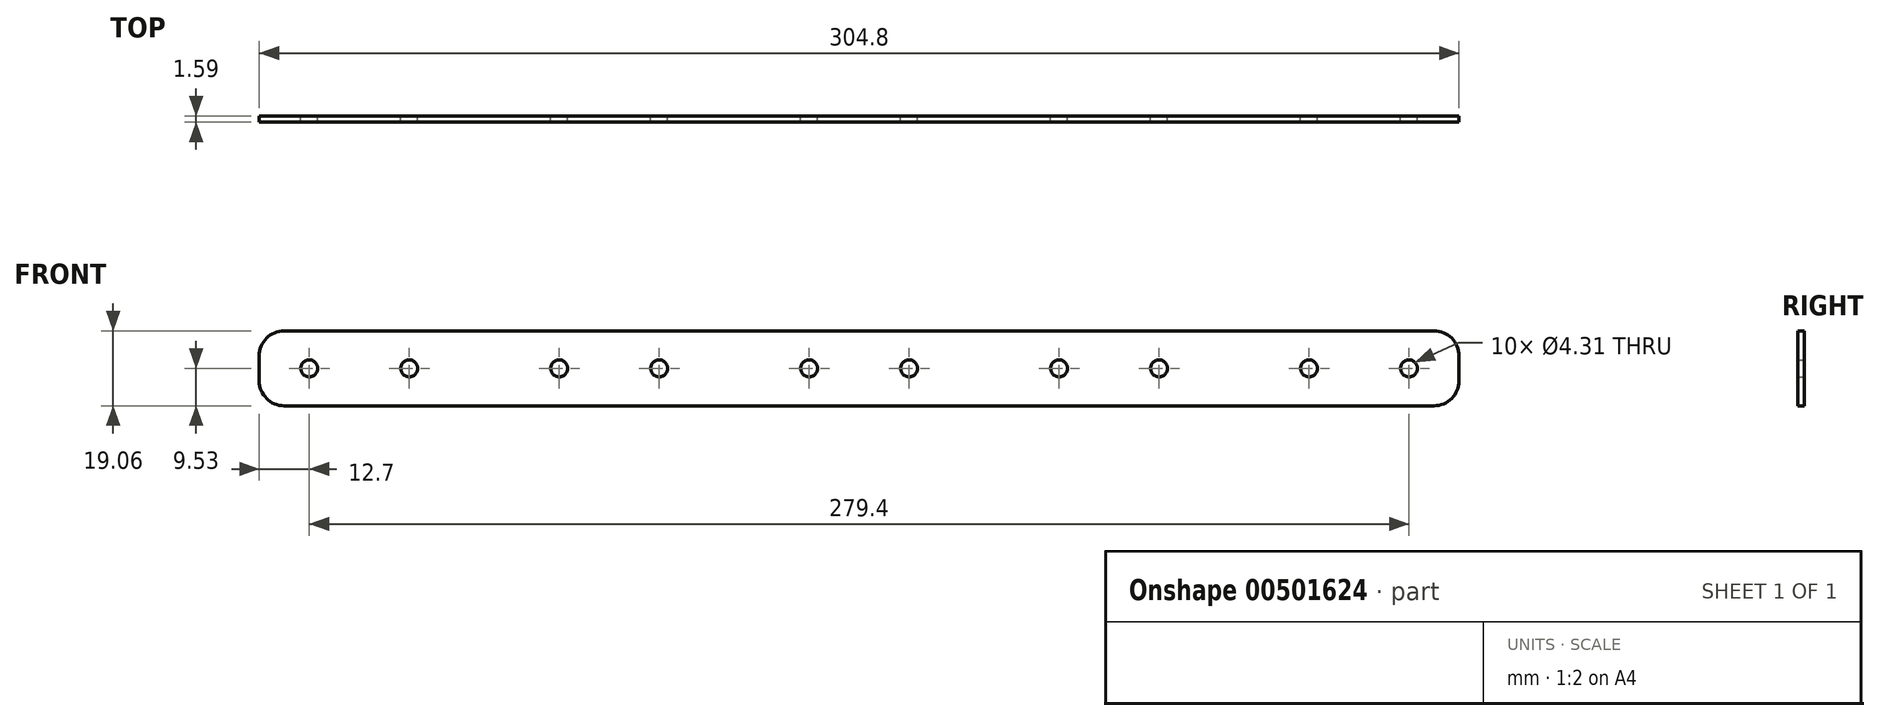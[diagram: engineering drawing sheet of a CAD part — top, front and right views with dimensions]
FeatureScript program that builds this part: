
annotation { "Feature Type Name" : "Feature", "Feature Type Description" : "" }
export const myFeature = defineFeature(function(context is Context, id is Id, definition is map)
    precondition{}
    {
        {
            var Q0;
            Q0=qCreatedBy(makeId("Front.planeOp"),FACE);
            var sketch = newSketch(context, id + "F0", { "sketchPlane" : qUnion([Q0])});
            skLineSegment(sketch, "E0.bottom", {"start": v(-146.05, 9.52) * mm, "end": v(146.05, 9.52) * mm});
            skLineSegment(sketch, "E0.top", {"start": v(-146.05, -9.53) * mm, "end": v(146.05, -9.53) * mm});
            skLineSegment(sketch, "E0.left", {"start": v(-152.4, 3.17) * mm, "end": v(-152.4, -3.18) * mm});
            skLineSegment(sketch, "E0.right", {"start": v(152.4, 3.17) * mm, "end": v(152.4, -3.18) * mm});
            skPoint(sketch, "E0.middle", {"position": v(0, 0) * mm});
            skCircle(sketch, "E1", {"center": v(-12.7, 0) * mm, "radius": 2.15 * mm});
            skCircle(sketch, "E2.MirrorC", {"center": v(12.7, 0) * mm, "radius": 2.15 * mm});
            skPoint(sketch, "E3.visualSharp", {"position": v(-152.4, 9.52) * mm});
            skArc(sketch, "E3.filletArc", {"start": v(-146.05, 9.52) * mm, "mid": v(-150.54, 7.67) * mm, "end": v(-152.4, 3.17) * mm});
            skPoint(sketch, "E4.visualSharp", {"position": v(-152.4, -9.53) * mm});
            skArc(sketch, "E4.filletArc", {"start": v(-152.4, -3.18) * mm, "mid": v(-150.54, -7.67) * mm, "end": v(-146.05, -9.53) * mm});
            skPoint(sketch, "E5.visualSharp", {"position": v(152.4, 9.52) * mm});
            skArc(sketch, "E5.filletArc", {"start": v(152.4, 3.17) * mm, "mid": v(150.54, 7.67) * mm, "end": v(146.05, 9.52) * mm});
            skPoint(sketch, "E6.visualSharp", {"position": v(152.4, -9.53) * mm});
            skArc(sketch, "E6.filletArc", {"start": v(146.05, -9.53) * mm, "mid": v(150.54, -7.67) * mm, "end": v(152.4, -3.18) * mm});
            skCircle(sketch, "E7.1.0.0", {"center": v(50.8, 0) * mm, "radius": 2.15 * mm});
            skCircle(sketch, "E7.1.0.1", {"center": v(76.2, 0) * mm, "radius": 2.15 * mm});
            skLineSegment(sketch, "E7.1.0.2", {"start": v(-82.55, -9.53) * mm, "end": v(209.55, -9.53) * mm});
            skCircle(sketch, "E7.2.0.0", {"center": v(114.3, 0) * mm, "radius": 2.15 * mm});
            skCircle(sketch, "E7.2.0.1", {"center": v(139.7, 0) * mm, "radius": 2.15 * mm});
            skLineSegment(sketch, "E7.2.0.2", {"start": v(-19.05, -9.53) * mm, "end": v(273.05, -9.53) * mm});
            skLineSegment(sketch, "E7.direction1", {"start": v(-12.7, 0) * mm, "end": v(50.8, 0) * mm, "construction": true});
            skCircle(sketch, "E8.MirrorC", {"center": v(-76.2, 0) * mm, "radius": 2.15 * mm});
            skCircle(sketch, "E9.MirrorC", {"center": v(-50.8, 0) * mm, "radius": 2.15 * mm});
            skCircle(sketch, "E10.MirrorC", {"center": v(-114.3, 0) * mm, "radius": 2.15 * mm});
            skCircle(sketch, "E11.MirrorC", {"center": v(-139.7, 0) * mm, "radius": 2.15 * mm});
            skSolve(sketch);
        }
        {
            var Q0;
            Q0=qSketchRegion(id+"F0",true);
            extrude(context, id + "F1", {"entities" : qUnion([Q0]), "depth" : 1.59 * mm});
        }
    });
